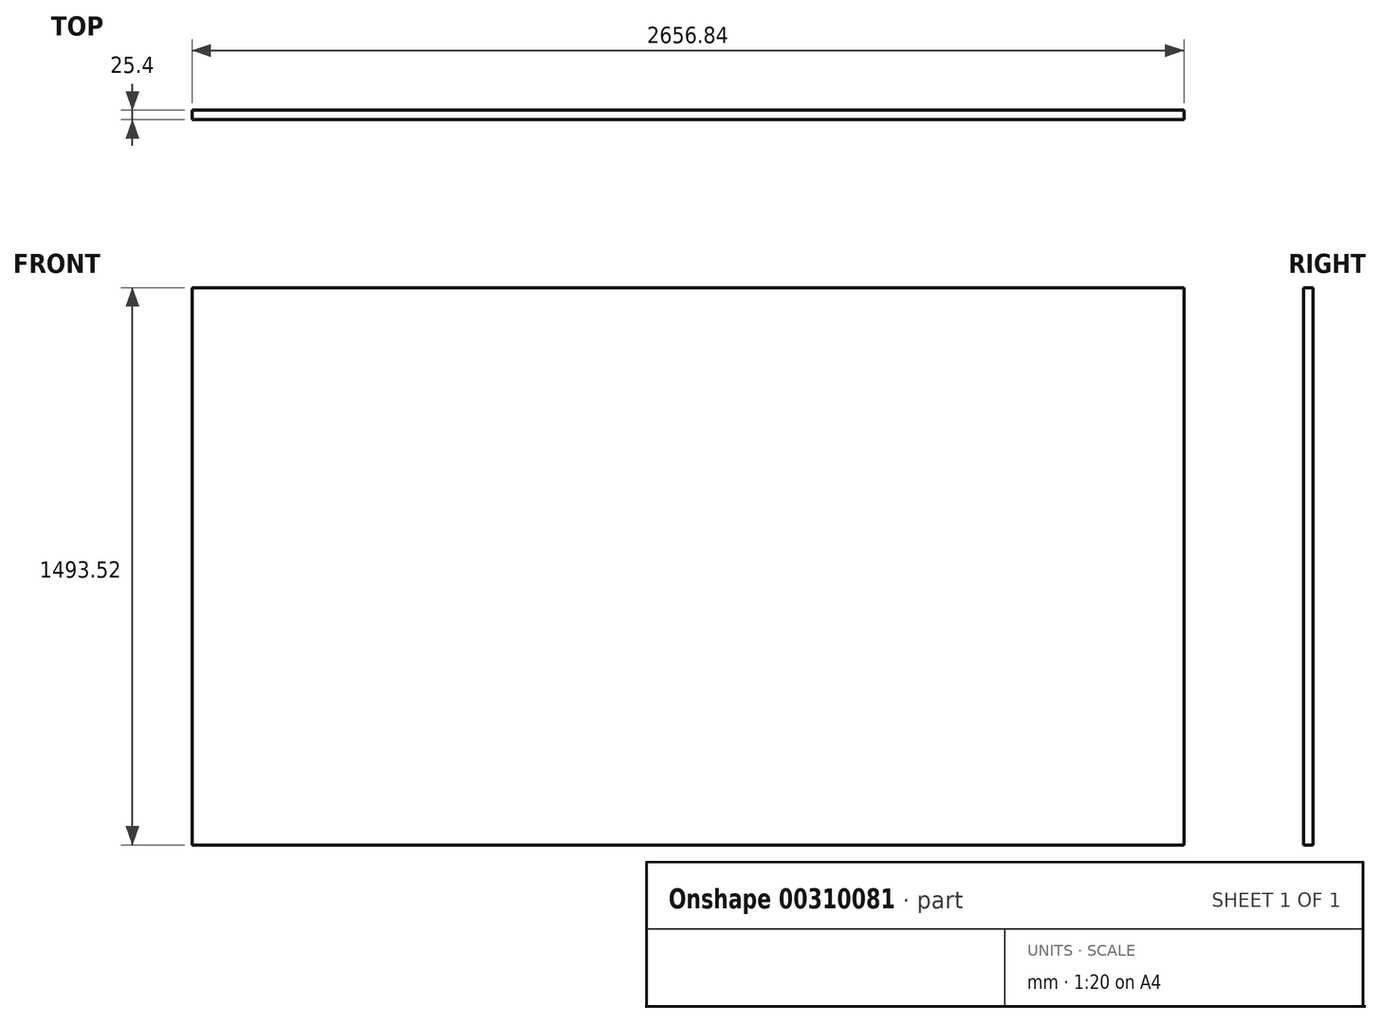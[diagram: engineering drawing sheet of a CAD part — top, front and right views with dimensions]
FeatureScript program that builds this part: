
annotation { "Feature Type Name" : "Feature", "Feature Type Description" : "" }
export const myFeature = defineFeature(function(context is Context, id is Id, definition is map)
    precondition{}
    {
        {
            var Q0;
            Q0=qCreatedBy(makeId("Front.planeOp"),FACE);
            var sketch = newSketch(context, id + "F0", { "sketchPlane" : qUnion([Q0])});
            skLineSegment(sketch, "E0.bottom", {"start": v(0, 1493.52) * mm, "end": v(2656.84, 1493.52) * mm});
            skLineSegment(sketch, "E0.top", {"start": v(0, 0) * mm, "end": v(2656.84, 0) * mm});
            skLineSegment(sketch, "E0.left", {"start": v(0, 1493.52) * mm, "end": v(0, 0) * mm});
            skLineSegment(sketch, "E0.right", {"start": v(2656.84, 1493.52) * mm, "end": v(2656.84, 0) * mm});
            skSolve(sketch);
        }
        {
            var Q0;
            Q0 = qSketchRegion(id + "F0", true);
            extrude(context, id + "F1", {"entities" : qUnion([Q0]), "depth" : 25.4 * mm});
        }
    });
